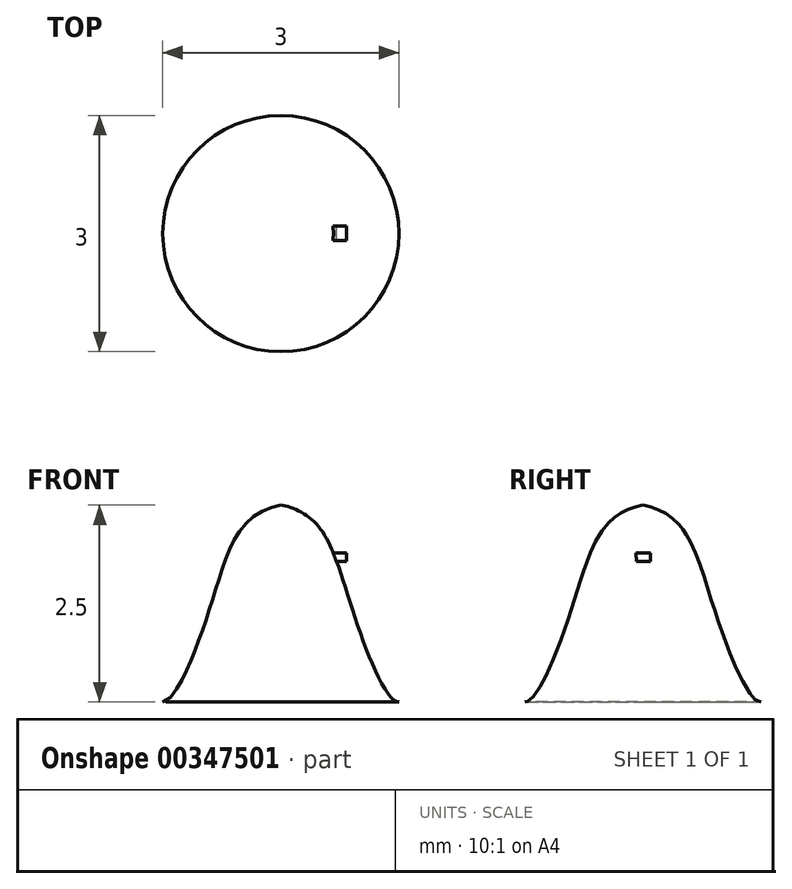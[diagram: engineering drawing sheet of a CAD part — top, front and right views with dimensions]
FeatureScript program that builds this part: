
annotation { "Feature Type Name" : "Feature", "Feature Type Description" : "" }
export const myFeature = defineFeature(function(context is Context, id is Id, definition is map)
    precondition{}
    {
        {
            var Q0;
            Q0=qCreatedBy(makeId("Front.planeOp"),FACE);
            var sketch = newSketch(context, id + "F0", { "sketchPlane" : qUnion([Q0])});
            skLineSegment(sketch, "E0", {"start": v(0, 2.5) * mm, "end": v(0, 0) * mm});
            skFitSpline(sketch, "E1", {"points": [v(0, 2.5) * mm, v(0.46, 2.25) * mm, v(0.94, 1.08) * mm, v(1.5, 0) * mm], "startDerivative": vector(1.7, -0.22) * mm, "endDerivative": vector(1.28, 0) * mm});
            skLineSegment(sketch, "E2", {"start": v(0, 0) * mm, "end": v(1.5, 0) * mm});
            skPoint(sketch, "E3", {"position": v(0.71, 1.77) * mm});
            skPoint(sketch, "E4", {"position": v(1.15, 0.52) * mm});
            skPoint(sketch, "E5", {"position": v(0.24, 2.42) * mm});
            skPoint(sketch, "E6", {"position": v(0.83, 1.4) * mm});
            skPoint(sketch, "E7", {"position": v(1.04, 0.78) * mm});
            skPoint(sketch, "E8", {"position": v(1.3, 0.19) * mm});
            skSolve(sketch);
        }
        {
            var Q0;
            Q0=makeQuery(id+"F0.imprint","IMPRINT",FACE,{"disambiguationData":[TD([[makeQuery(id+"F0.imprint","IMPRINT",EDGE,{"derivedFrom":sQuery(id+"F0.wireOp",EDGE,"E0")}),1.0]])]});
            var Q1;
            Q1=sQuery(id+"F0.wireOp",EDGE,"E0");
            revolve(context, id + "F1", {"entities" : qUnion([Q0]), "axis" : qUnion([Q1]), "revolveType" : RevolveType.FULL});
        }
        {
            var Q0;
            Q0=qCreatedBy(makeId("Right.planeOp"),FACE);
            var sketch = newSketch(context, id + "F2", { "sketchPlane" : qUnion([Q0])});
            skLineSegment(sketch, "E9", {"start": v(-0.1, 1.9) * mm, "end": v(0.1, 1.9) * mm});
            skLineSegment(sketch, "E10", {"start": v(0.1, 1.9) * mm, "end": v(0.1, 1.79) * mm});
            skLineSegment(sketch, "E11", {"start": v(0.1, 1.79) * mm, "end": v(-0.08, 1.79) * mm});
            skLineSegment(sketch, "E12", {"start": v(-0.08, 1.79) * mm, "end": v(-0.1, 1.9) * mm});
            skSolve(sketch);
        }
        {
            var Q0;
            Q0 = qSketchRegion(id + "F2", true);
            extrude(context, id + "F3", {"entities" : qUnion([Q0]), "operationType" : NewBodyOperationType.ADD, "depth" : 0.84 * mm});
        }
    });
